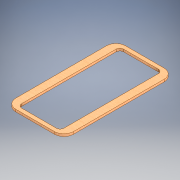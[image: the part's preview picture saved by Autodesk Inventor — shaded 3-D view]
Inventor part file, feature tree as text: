
AUTODESK INVENTOR PART (.ipt)
format: ipt  version: 2020 (Build 240168000, 168)  size: 145,920 bytes
history: native  units: mm
features: extrude x1
ambient origin geometry x8: Origin, YZ Plane, XZ Plane, XY Plane, X Axis, Y Axis, Z Axis, Center Point
bodies: Solide1 (feature_tree)
feature tree (1):
  extrude  "Extrusion1"  Depth=150.0mm
